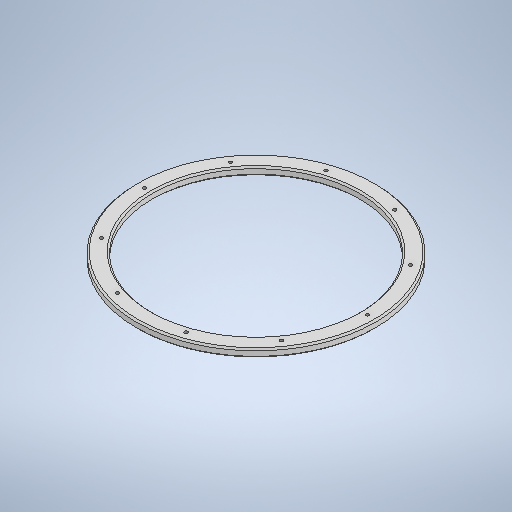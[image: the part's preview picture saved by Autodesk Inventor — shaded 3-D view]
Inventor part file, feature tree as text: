
AUTODESK INVENTOR PART (.ipt)
format: ipt  version: 2025.1 (Build 291241000, 241)  size: 302,592 bytes
history: native  units: mm
features: sketch x2, other x1, revolve x1, chamfer x1, hole x1, pattern_circular x1
ambient origin geometry x8: Origin, YZ Plane, XZ Plane, XY Plane, X Axis, Y Axis, Z Axis, Center Point
bodies: Body1 (feature_tree)
feature tree (7):
  other  "Sólido1"
  revolve  "Revolución1"  [1 undecoded]
  chamfer  "Chaflán1"  Angle=90.0deg  [1 undecoded]
  hole  "Agujero1"  [1 undecoded]
  pattern_circular  "Patrón circular1"  [2 undecoded]
  sketch  "Boceto1"  dims[d0=20.0mm d1=10.0mm]
  sketch  "Boceto2"  dims[d2=150.0mm d3=90.0deg d4=2.0mm d5=2.0mm d6=45.0deg d7=4.134mm d8=10.0mm d9=4.0mm d10=2.0mm d11=90.0deg d12=0.5mm d13=20.594885mm d14=100.0mm d15=360.0deg]
note: 5 required parameter values undecoded (feature->parameter linkage not recoverable at this tier; creation-order binding heuristic only, values carry confidence <= 0.55)